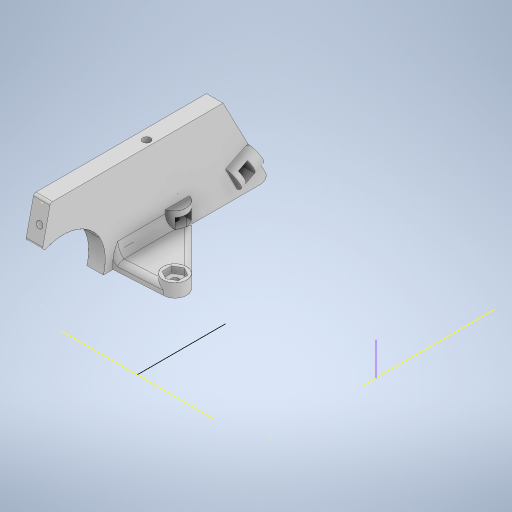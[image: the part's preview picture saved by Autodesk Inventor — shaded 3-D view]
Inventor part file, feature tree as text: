
AUTODESK INVENTOR PART (.ipt)
format: ipt  version: 2023 (Build 270158000, 158)  size: 3,086,336 bytes
history: native  units: mm
features: projected_geometry x136, extrude x122, sketch x90, fillet x11, reference x5, plane x3, mirror x3, other x3
ambient origin geometry x8: Origin, YZ Plane, XZ Plane, XY Plane, X Axis, Y Axis, Z Axis, Center Point
bodies: Solid1 (feature_tree)
feature tree (373):
  sketch  "Sketch1"  dims[d0=100.0mm d1=100.0mm]
  extrude  "Extrusion1"  Depth=100.0mm
  extrude  "Extrusion2"  Depth=20.0mm
  extrude  "Extrusion3"  Depth=20.0mm
  sketch  "Sketch3"  dims[d4=31.0mm d5=20.0mm]
  extrude  "Extrusion4"  Depth=19.0mm
  extrude  "Extrusion5"  Depth=10.0mm
  sketch  "Sketch4"  dims[d6=14.0mm d7=19.0mm]
  plane  "Work Plane1"
  mirror  "Mirror1"
  extrude  "Extrusion6"  Depth=10.0mm
  sketch  "Sketch8"  dims[d10=10.0mm d11=2.0mm]
  extrude  "Extrusion7"  Depth=15.0mm
  extrude  "Extrusion8"  Depth=2.0mm
  extrude  "Extrusion9"  Depth=1.0mm
  sketch  "Sketch9"  dims[d12=2.0mm d13=15.0mm]
  extrude  "Extrusion10"  Depth=10.0mm TaperAngle=0.0deg
  extrude  "Extrusion11"  TaperAngle=0.0deg  [1 undecoded]
  sketch  "Sketch10"  dims[d14=15.0mm d15=2.0mm]
  extrude  "Extrusion12"  Depth=14.0mm TaperAngle=0.0deg
  extrude  "Extrusion13"  TaperAngle=90.0deg  [1 undecoded]
  extrude  "Extrusion14"  Depth=40.0mm
  sketch  "Sketch12"  dims[d18=10.0mm d19=0.0mm d20=2.0mm d21=0.0mm]
  extrude  "Extrusion15"  Depth=25.0mm
  extrude  "Extrusion16"  Depth=5.0mm
  extrude  "Extrusion17"  Depth=13.0mm
  extrude  "Extrusion18"  Depth=8.0mm
  extrude  "Extrusion19"  Depth=18.0mm TaperAngle=0.0deg
  extrude  "Extrusion20"  Depth=49.0mm
  extrude  "Extrusion21"  Depth=5.0mm
  sketch  "Sketch15"  dims[d28=14.25mm d29=0.0mm d30=90.0deg]
  plane  "Work Plane2"
  mirror  "Mirror2"
  extrude  "Extrusion22"  TaperAngle=0.0deg  [1 undecoded]
  sketch  "Sketch17"  dims[d36=15.0mm d37=25.0mm]
  extrude  "Extrusion23"  Depth=10.0mm
  extrude  "Extrusion24"  Depth=1.6mm
  extrude  "Extrusion25"  TaperAngle=0.0deg  [1 undecoded]
  extrude  "Extrusion26"  Depth=14.0mm TaperAngle=0.0deg
  extrude  "Extrusion27"  Depth=6.0mm
  sketch  "Sketch21"  dims[d44=18.0mm d45=0.0mm d46=18.0mm d47=0.0mm]
  extrude  "Extrusion28"  Depth=2.0mm
  extrude  "Extrusion29"  Depth=6.0mm TaperAngle=0.0deg
  sketch  "Sketch22"  dims[d48=0.0mm d49=0.0mm d50=49.0mm]
  extrude  "Extrusion30"  Depth=15.0mm TaperAngle=0.0deg
  extrude  "Extrusion31"  Depth=3.2mm
  extrude  "Extrusion32"  Depth=4.0mm
  extrude  "Extrusion33"  Depth=1.0mm TaperAngle=0.0deg
  extrude  "Extrusion34"  Depth=3.0mm
  extrude  "Extrusion35"  Depth=15.0mm TaperAngle=0.0deg
  extrude  "Extrusion36"  Depth=3.2mm
  fillet  "Face Fillet1"
  fillet  "Face Fillet2"
  extrude  "Extrusion37"  Depth=3.2mm
  fillet  "Face Fillet3"
  fillet  "Face Fillet5"
  extrude  "Extrusion38"  Depth=5.0mm TaperAngle=0.0deg
  extrude  "Extrusion39"  TaperAngle=0.0deg  [1 undecoded]
  fillet  "Fillet2"  Radius=2.8mm
  extrude  "Extrusion40"  Depth=100.0mm TaperAngle=0.0deg
  sketch  "Sketch32"  dims[d76=6.0mm d77=0.0mm d78=15.0mm d79=0.0mm]
  extrude  "Extrusion41"  Depth=11.0mm
  extrude  "Extrusion42"  Depth=9.0mm TaperAngle=0.0deg
  extrude  "Extrusion43"  Depth=3.2mm
  sketch  "Sketch33"  dims[d80=15.0mm d81=0.0mm d82=3.2mm]
  extrude  "Extrusion44"  Depth=7.0mm TaperAngle=0.0deg
  extrude  "Extrusion45"  Depth=40.656mm TaperAngle=0.0deg
  extrude  "Extrusion46"  Depth=9.0mm TaperAngle=0.0deg
  extrude  "Extrusion47"  Depth=3.0mm
  sketch  "Sketch36"  dims[d91=90.0deg d92=3.0mm]
  extrude  "Extrusion48"  Depth=1.5mm TaperAngle=0.0deg
  extrude  "Extrusion49"  Depth=6.0mm
  sketch  "Sketch37"  dims[d93=3.0mm d94=15.0mm d95=0.0mm]
  extrude  "Extrusion50"  Depth=10.0mm TaperAngle=0.0deg
  extrude  "Extrusion51"  Depth=4.0mm
  extrude  "Extrusion52"  Depth=10.0mm TaperAngle=0.0deg
  extrude  "Extrusion53"  Depth=20.0mm TaperAngle=0.0deg
  sketch  "Sketch40"  dims[d100=4.0mm d101=5.0mm d102=0.0mm]
  extrude  "Extrusion54"  Depth=1.5mm
  extrude  "Extrusion55"  Depth=3.0mm
  extrude  "Extrusion56"  Depth=6.4mm
  extrude  "Extrusion57"  Depth=3.0mm
  fillet  "Fillet3"  Radius=2.0mm
  extrude  "Extrusion58"  TaperAngle=0.0deg  [1 undecoded]
  sketch  "Sketch44"  dims[d114=3.4mm d115=9.0mm d116=0.0mm]
  extrude  "Extrusion59"  TaperAngle=0.0deg  [1 undecoded]
  extrude  "Extrusion60"  Depth=10.0mm TaperAngle=0.0deg
  sketch  "Sketch45"  dims[d117=15.0mm d118=0.0mm d119=3.2mm]
  extrude  "Extrusion61"  Depth=10.0mm TaperAngle=0.0deg
  extrude  "Extrusion62"  Depth=3.0mm
  sketch  "Sketch46"  dims[d120=3.2mm d121=7.0mm d122=0.0mm]
  extrude  "Extrusion63"  Depth=6.5mm TaperAngle=0.0deg
  extrude  "Extrusion64"  Depth=17.0mm TaperAngle=0.0deg
  extrude  "Extrusion65"  Depth=3.0mm
  extrude  "Extrusion66"  Depth=5.0mm TaperAngle=0.0deg
  sketch  "Sketch49"  dims[d138=28.734mm d139=3.0mm]
  extrude  "Extrusion67"  Depth=6.5mm TaperAngle=0.0deg
  extrude  "Extrusion68"  Depth=14.0mm TaperAngle=0.0deg
  extrude  "Extrusion69"  Depth=6.5mm
  extrude  "Extrusion70"  Depth=6.5mm TaperAngle=0.0deg
  extrude  "Extrusion71"  Depth=17.0mm TaperAngle=0.0deg
  extrude  "Extrusion72"  Depth=2.5mm
  extrude  "Extrusion73"  Depth=2.0mm
  extrude  "Extrusion74"  TaperAngle=0.0deg  [1 undecoded]
  extrude  "Extrusion75"  Depth=6.5mm TaperAngle=0.0deg
  extrude  "Extrusion76"  Depth=1.0mm
  sketch  "Sketch53"  dims[d149=6.7mm d152=4.0mm]
  extrude  "Extrusion77"  Depth=1.0mm
  extrude  "Extrusion78"  Depth=3.0mm
  extrude  "Extrusion79"  Depth=15.0mm TaperAngle=0.0deg
  extrude  "Extrusion80"  Depth=10.0mm TaperAngle=0.0deg
  extrude  "Extrusion81"  Depth=10.0mm TaperAngle=0.0deg
  extrude  "Extrusion82"  Depth=4.0mm TaperAngle=0.0deg
  extrude  "Extrusion83"  Depth=10.0mm TaperAngle=0.0deg
  sketch  "Sketch59"  dims[d166=6.4mm d167=3.0mm d169=2.0mm]
  extrude  "Extrusion84"  Depth=7.0mm
  extrude  "Extrusion85"  Depth=6.5mm TaperAngle=0.0deg
  extrude  "Extrusion86"  Depth=4.0mm TaperAngle=0.0deg
  extrude  "Extrusion87"  Depth=1.0mm
  extrude  "Extrusion88"  Depth=10.0mm TaperAngle=0.0deg
  sketch  "Sketch62"  dims[d178=10.0mm d179=0.0mm d180=4.0mm d181=0.0mm]
  extrude  "Extrusion89"  Depth=10.0mm
  extrude  "Extrusion90"  Depth=10.0mm
  fillet  "Fillet4"  Radius=30.0mm
  extrude  "Extrusion91"  Depth=10.0mm
  extrude  "Extrusion92"  Depth=10.0mm
  extrude  "Extrusion93"  Depth=10.0mm TaperAngle=0.0deg
  extrude  "Extrusion94"  TaperAngle=135.0deg  [1 undecoded]
  extrude  "Extrusion95"  TaperAngle=0.0deg  [1 undecoded]
  sketch  "Sketch68"  dims[d205=4.0mm d206=0.0mm d207=5.0mm d208=0.0mm]
  extrude  "Extrusion96"  Depth=10.0mm TaperAngle=0.0deg
  extrude  "Extrusion97"  Depth=10.0mm
  extrude  "Extrusion98"  Depth=10.0mm
  extrude  "Extrusion99"  Depth=10.0mm
  extrude  "Extrusion100"  TaperAngle=0.0deg  [1 undecoded]
  sketch  "Sketch74"  dims[d219=6.5mm d220=0.0mm d221=16.0mm d222=0.0mm]
  extrude  "Extrusion101"  Depth=1.0mm TaperAngle=0.0deg
  extrude  "Extrusion102"  Depth=10.0mm TaperAngle=0.0deg
  extrude  "Extrusion103"  Depth=10.0mm TaperAngle=0.0deg
  extrude  "Extrusion104"  Depth=10.0mm TaperAngle=0.0deg
  extrude  "Extrusion105"  Depth=10.0mm TaperAngle=0.0deg
  fillet  "Fillet6"  Radius=12.0mm
  fillet  "Fillet7"  Radius=2.0mm
  extrude  "Extrusion106"  Depth=10.0mm TaperAngle=0.0deg
  fillet  "Fillet8"  Radius=5.0mm
  extrude  "Extrusion107"  Depth=6.5mm TaperAngle=0.0deg
  sketch  "Sketch80"  dims[d239=1.0mm d240=2.5mm]
  extrude  "Extrusion108"  Depth=10.0mm
  extrude  "Extrusion109"  Depth=10.0mm TaperAngle=0.0deg
  extrude  "Extrusion110"  Depth=10.0mm TaperAngle=0.0deg
  extrude  "Extrusion111"  Depth=10.0mm
  extrude  "Extrusion112"  Depth=10.0mm
  fillet  "Fillet9"  Radius=3.5mm
  extrude  "Extrusion113"  Depth=10.0mm
  extrude  "Extrusion114"  Depth=6.5mm TaperAngle=0.0deg
  extrude  "Extrusion115"  Depth=6.5mm TaperAngle=0.0deg
  plane  "Work Plane3"
  mirror  "Mirror3"
  extrude  "Extrusion116"  Depth=10.0mm
  extrude  "Extrusion117"  Depth=10.0mm TaperAngle=0.0deg
  sketch  "Sketch89"  dims[d269=6.5mm d270=0.0mm d271=3.0mm d272=0.0mm]
  extrude  "Extrusion118"  Depth=10.0mm TaperAngle=0.0deg
  extrude  "Extrusion119"  Depth=10.0mm
  extrude  "Wyciągnięcie proste120"  TaperAngle=90.0deg  [1 undecoded]
  extrude  "Wyciągnięcie proste121"  Depth=10.0mm
  extrude  "Wyciągnięcie proste122"  Depth=10.0mm TaperAngle=0.0deg
  sketch  "Sketch2"  dims[d2=5.0mm d3=20.0mm]
  projected_geometry  "Projected Loop1"
  sketch  "Sketch6"  dims[d8=10.0mm d9=14.0mm]
  projected_geometry  "Projected Loop5"
  projected_geometry  "Projected Loop6"
  projected_geometry  "Projected Loop7"
  projected_geometry  "Projected Loop8"
  projected_geometry  "Projected Loop9"
  projected_geometry  "Projected Loop10"
  sketch  "Sketch11"  dims[d16=1.0mm d17=5.0mm]
  projected_geometry  "Projected Loop11"
  projected_geometry  "Projected Loop12"
  sketch  "Sketch13"  dims[d22=31.0mm d23=0.0mm d24=0.0mm]
  projected_geometry  "Projected Loop13"
  projected_geometry  "Projected Loop14"
  sketch  "Sketch14"  dims[d25=30.4mm d26=14.0mm d27=0.0mm]
  projected_geometry  "Projected Loop15"
  projected_geometry  "Projected Loop16"
  sketch  "Sketch16"  dims[d33=25.0mm d34=0.0mm d35=40.0mm]
  projected_geometry  "Projected Loop17"
  projected_geometry  "Projected Loop18"
  projected_geometry  "Projected Loop19"
  sketch  "Sketch18"  dims[d38=20.0mm d39=5.0mm]
  projected_geometry  "Projected Loop20"
  projected_geometry  "Projected Loop21"
  projected_geometry  "Projected Loop22"
  projected_geometry  "Projected Loop23"
  projected_geometry  "Projected Loop24"
  projected_geometry  "Projected Loop25"
  projected_geometry  "Projected Loop26"
  sketch  "Sketch19"  dims[d40=7.0mm d41=13.0mm]
  projected_geometry  "Projected Loop27"
  sketch  "Sketch20"  dims[d42=7.0mm d43=8.0mm]
  projected_geometry  "Projected Loop28"
  projected_geometry  "Projected Loop29"
  projected_geometry  "Projected Loop30"
  sketch  "Sketch23"  dims[d51=25.0mm d52=5.0mm]
  sketch  "Sketch24"  dims[d53=20.0mm d54=0.0mm d55=0.0mm]
  projected_geometry  "Projected Loop31"
  projected_geometry  "Projected Loop32"
  sketch  "Sketch25"  dims[d56=10.0mm d57=0.0mm d58=1.6mm]
  projected_geometry  "Projected Loop33"
  sketch  "Sketch26"  dims[d59=1.6mm d60=1.6mm]
  projected_geometry  "Projected Loop34"
  sketch  "Sketch27"  dims[d61=5.0mm d62=0.0mm d63=0.0mm d64=0.0mm]
  projected_geometry  "Projected Loop35"
  sketch  "Sketch28"  dims[d65=2.5mm d66=14.0mm d67=0.0mm]
  projected_geometry  "Projected Loop36"
  sketch  "Sketch29"  dims[d68=2.0mm d69=6.0mm]
  sketch  "Sketch30"  dims[d70=5.0mm d71=2.0mm]
  projected_geometry  "Projected Loop37"
  projected_geometry  "Projected Loop38"
  projected_geometry  "Projected Loop39"
  sketch  "Sketch31"  dims[d72=14.0mm d73=0.0mm d74=6.0mm d75=0.0mm]
  projected_geometry  "Projected Loop40"
  projected_geometry  "Projected Loop41"
  projected_geometry  "Projected Loop42"
  projected_geometry  "Projected Loop43"
  projected_geometry  "Projected Loop44"
  projected_geometry  "Projected Loop45"
  projected_geometry  "Projected Loop46"
  sketch  "Sketch34"  dims[d83=3.2mm d84=4.0mm]
  projected_geometry  "Projected Loop47"
  projected_geometry  "Projected Loop48"
  sketch  "Sketch35"  dims[d85=15.0mm d86=0.0mm d87=1.0mm d88=0.0mm]
  projected_geometry  "Projected Loop49"
  projected_geometry  "Projected Loop50"
  projected_geometry  "Projected Loop51"
  projected_geometry  "Projected Loop52"
  projected_geometry  "Projected Loop53"
  sketch  "Sketch38"  dims[d96=3.2mm d97=3.2mm]
  projected_geometry  "Projected Loop54"
  projected_geometry  "Projected Loop55"
  sketch  "Sketch39"  dims[d98=3.2mm d99=3.2mm]
  projected_geometry  "Projected Loop56"
  sketch  "Sketch41"  dims[d103=5.0mm d104=0.0mm d105=0.0mm d106=0.0mm d107=2.8mm]
  projected_geometry  "Projected Loop57"
  sketch  "Sketch42"  dims[d108=2.8mm d109=100.0mm d110=0.0mm]
  projected_geometry  "Projected Loop58"
  sketch  "Sketch43"  dims[d111=20.0mm d112=0.0mm d113=11.0mm]
  projected_geometry  "Projected Loop59"
  projected_geometry  "Projected Loop60"
  projected_geometry  "Projected Loop61"
  projected_geometry  "Projected Loop62"
  projected_geometry  "Projected Loop63"
  projected_geometry  "Projected Loop64"
  projected_geometry  "Projected Loop65"
  projected_geometry  "Projected Loop66"
  projected_geometry  "Projected Loop67"
  projected_geometry  "Projected Loop68"
  projected_geometry  "Projected Loop69"
  projected_geometry  "Projected Loop70"
  projected_geometry  "Projected Loop71"
  projected_geometry  "Projected Loop72"
  projected_geometry  "Projected Loop73"
  projected_geometry  "Projected Loop74"
  projected_geometry  "Projected Loop75"
  projected_geometry  "Projected Loop76"
  projected_geometry  "Projected Loop77"
  projected_geometry  "Projected Loop78"
  sketch  "Sketch47"  dims[d123=4.0mm d124=0.0mm d125=40.656mm d126=0.0mm]
  projected_geometry  "Projected Loop79"
  sketch  "Sketch48"  dims[d127=3.0mm d128=0.0mm d129=9.0mm d130=0.0mm]
  projected_geometry  "Projected Loop80"
  projected_geometry  "Projected Loop81"
  sketch  "Sketch50"  dims[d140=1.5mm d141=0.0mm d142=1.5mm d143=0.0mm]
  projected_geometry  "Projected Loop82"
  projected_geometry  "Projected Loop83"
  sketch  "Sketch51"  dims[d144=6.0mm d145=6.0mm]
  projected_geometry  "Projected Loop84"
  sketch  "Sketch52"  dims[d146=2.0mm d147=10.0mm d148=0.0mm]
  projected_geometry  "Projected Loop85"
  projected_geometry  "Projected Loop86"
  projected_geometry  "Projected Loop87"
  sketch  "Sketch54"  dims[d153=10.0mm d154=0.0mm d155=16.0mm d156=0.0mm]
  projected_geometry  "Projected Loop88"
  projected_geometry  "Projected Loop89"
  sketch  "Sketch55"  dims[d157=1e-05mm d158=20.0mm d159=0.0mm]
  projected_geometry  "Projected Loop90"
  projected_geometry  "Projected Loop91"
  sketch  "Sketch56"  dims[d160=6.4mm d161=1.5mm]
  projected_geometry  "Projected Loop92"
  projected_geometry  "Projected Loop93"
  projected_geometry  "Projected Loop94"
  sketch  "Sketch57"  dims[d162=16.5mm d163=3.0mm]
  projected_geometry  "Projected Loop95"
  projected_geometry  "Projected Loop96"
  projected_geometry  "Projected Loop97"
  sketch  "Sketch58"  dims[d164=3.0mm d165=6.4mm]
  projected_geometry  "Projected Loop98"
  projected_geometry  "Projected Loop99"
  projected_geometry  "Projected Loop100"
  projected_geometry  "Projected Loop101"
  sketch  "Sketch60"  dims[d170=5.928mm d171=0.0mm d172=0.0mm d173=0.0mm]
  projected_geometry  "Projected Loop102"
  projected_geometry  "Projected Loop103"
  sketch  "Sketch61"  dims[d174=3.0mm d175=0.0mm d176=0.0mm d177=0.0mm]
  projected_geometry  "Projected Loop104"
  projected_geometry  "Projected Loop105"
  projected_geometry  "Projected Loop106"
  projected_geometry  "Projected Loop107"
  projected_geometry  "Projected Loop108"
  projected_geometry  "Projected Loop109"
  projected_geometry  "Projected Loop110"
  projected_geometry  "Projected Loop111"
  sketch  "Sketch63"  dims[d182=2.5mm d183=10.0mm d184=0.0mm]
  projected_geometry  "Projected Loop112"
  sketch  "Sketch64"  dims[d185=2.0mm d186=3.0mm]
  projected_geometry  "Projected Loop113"
  sketch  "Sketch65"  dims[d195=0.0mm d196=0.0mm d197=6.5mm d198=0.0mm]
  projected_geometry  "Projected Loop114"
  reference  "Reference1"
  sketch  "Sketch66"  dims[d199=2.5mm d200=17.0mm d201=0.0mm]
  reference  "Reference2"
  reference  "Reference3"
  sketch  "Sketch67"  dims[d202=14.0mm d203=0.0mm d204=3.0mm]
  projected_geometry  "Projected Loop115"
  projected_geometry  "Projected Loop116"
  sketch  "Sketch69"  dims[d209=2.5mm d210=6.5mm d211=0.0mm]
  projected_geometry  "Projected Loop117"
  sketch  "Sketch72"  dims[d212=0.0mm d213=0.0mm d214=14.0mm d215=0.0mm]
  projected_geometry  "Projected Loop118"
  sketch  "Sketch73"  dims[d216=6.5mm d217=0.0mm d218=2.0mm]
  projected_geometry  "Projected Loop119"
  projected_geometry  "Projected Loop120"
  sketch  "Sketch75"  dims[d223=17.0mm d224=0.0mm d225=17.0mm d226=0.0mm]
  reference  "Reference4"
  projected_geometry  "Projected Loop121"
  sketch  "Sketch76"  dims[d227=17.0mm d228=0.0mm d229=2.5mm]
  projected_geometry  "Projected Loop122"
  sketch  "Sketch77"  dims[d230=2.5mm d231=2.0mm]
  projected_geometry  "Projected Loop123"
  sketch  "Sketch78"  dims[d232=13.0mm d233=0.0mm d234=0.0mm]
  projected_geometry  "Projected Loop124"
  sketch  "Sketch79"  dims[d235=6.5mm d236=0.0mm d237=3.0mm d238=0.0mm]
  projected_geometry  "Projected Loop125"
  projected_geometry  "Projected Loop126"
  projected_geometry  "Projected Loop127"
  sketch  "Sketch81"  dims[d241=14.0mm d242=0.0mm d243=1.0mm]
  sketch  "Sketch82"  dims[d244=2.0mm d245=3.0mm]
  projected_geometry  "Projected Loop128"
  sketch  "Sketch83"  dims[d246=3.2mm d247=15.0mm d248=0.0mm]
  projected_geometry  "Projected Loop129"
  projected_geometry  "Projected Loop130"
  sketch  "Sketch84"  dims[d249=10.0mm d250=0.0mm d251=10.0mm d252=0.0mm]
  projected_geometry  "Projected Loop131"
  reference  "Reference5"
  projected_geometry  "Projected Loop132"
  sketch  "Sketch85"  dims[d253=3.0mm d254=0.0mm d255=10.0mm d256=0.0mm]
  sketch  "Sketch86"  dims[d257=8.0mm d258=0.0mm d259=4.0mm d260=0.0mm]
  sketch  "Sketch87"  dims[d261=2.5mm d262=10.0mm d263=0.0mm]
  projected_geometry  "Projected Loop133"
  projected_geometry  "Projected Loop134"
  sketch  "Sketch88"  dims[d266=7.0mm d268=7.0mm]
  projected_geometry  "Projected Loop135"
  sketch  "Sketch90"  dims[d273=8.0mm d274=0.0mm d275=4.0mm d276=0.0mm]
  sketch  "Sketch91"  dims[d277=1.0mm d278=1.0mm d279=10.0mm d280=0.0mm d281=1.308997mm d282=45.0mm d283=30.0mm d284=0.0mm d285=2.0mm d286=2.5mm d287=11.0mm d288=0.0mm d289=135.0deg d290=0.0mm d291=0.0mm d292=3.7mm d293=0.0mm d294=10.0mm d295=6.4mm d296=3.0mm d297=0.0mm d298=0.0mm d299=1.0mm d300=0.0mm d301=1.5mm d302=0.0mm d303=5.928mm d304=0.0mm d305=12.0mm d306=0.0mm d307=12.0mm d308=0.0mm d309=12.0mm d310=0.0mm d311=2.0mm d312=41.5mm d313=0.0mm d314=5.0mm d315=0.0mm d316=6.5mm d317=0.0mm d318=2.5mm d319=15.0mm d320=0.0mm d321=15.0mm d322=0.0mm d323=6.4mm d324=1.5mm d325=3.5mm d326=3.5mm d327=6.5mm d328=0.0mm d329=6.5mm d330=0.0mm d331=1.047198mm d332=11.908mm d333=0.0mm d334=12.0mm d335=0.0mm d336=8.0mm d337=90.0deg d338=2.7mm d339=10.0mm d340=0.0mm d341=6.4mm d342=10.0mm d343=0.0mm d344=6.5mm d345=0.0mm d346=6.5mm d347=0.0mm d348=6.5mm d349=0.0mm d350=6.5mm d351=0.0mm d353=1.0mm d354=1.0mm d355=6.5mm d356=0.0mm d357=1.0mm d358=2.0mm d359=6.5mm d360=0.0mm d361=4.0mm d362=0.0mm d363=4.0mm d364=0.0mm d365=44.0mm d366=0.0mm d367=6.5mm d368=0.0mm d369=6.5mm d370=0.0mm d371=1.0mm d372=4.0mm d373=10.0mm d374=0.0mm d375=15.0mm d376=0.0mm d377=12.0mm d378=0.0mm d379=41.75mm d380=6.0mm d381=6.0mm d382=6.5mm d383=0.0mm d384=4.0mm d385=0.0mm d386=0.0mm d387=0.0mm d388=1.5mm d389=1.5mm d390=10.0mm d391=0.0mm d392=10.0mm d393=0.0mm d394=10.0mm d395=0.0mm d396=0.0mm d397=0.0mm d150=0.0mm d151=0.0mm d352=0.0mm]
  projected_geometry  "Projected Loop136"
  sketch  "Szkic92"
  projected_geometry  "Pętla rzutowana137"
  sketch  "Szkic93"
  projected_geometry  "Pętla rzutowana138"
  sketch  "Szkic94"
  projected_geometry  "Pętla rzutowana139"
  parser-record x1  (decoder bookkeeping rows leaked as tree rows — omitted from the tree; the rows remain in map.json)
  other  "zlozenie.iam"
  other  "sciana_lewa_v4:1"
note: 12 required parameter values undecoded (feature->parameter linkage not recoverable at this tier; creation-order binding heuristic only, values carry confidence <= 0.55)
note: 1 file-system path scrubbed to <path> (originals preserved in map.json)
